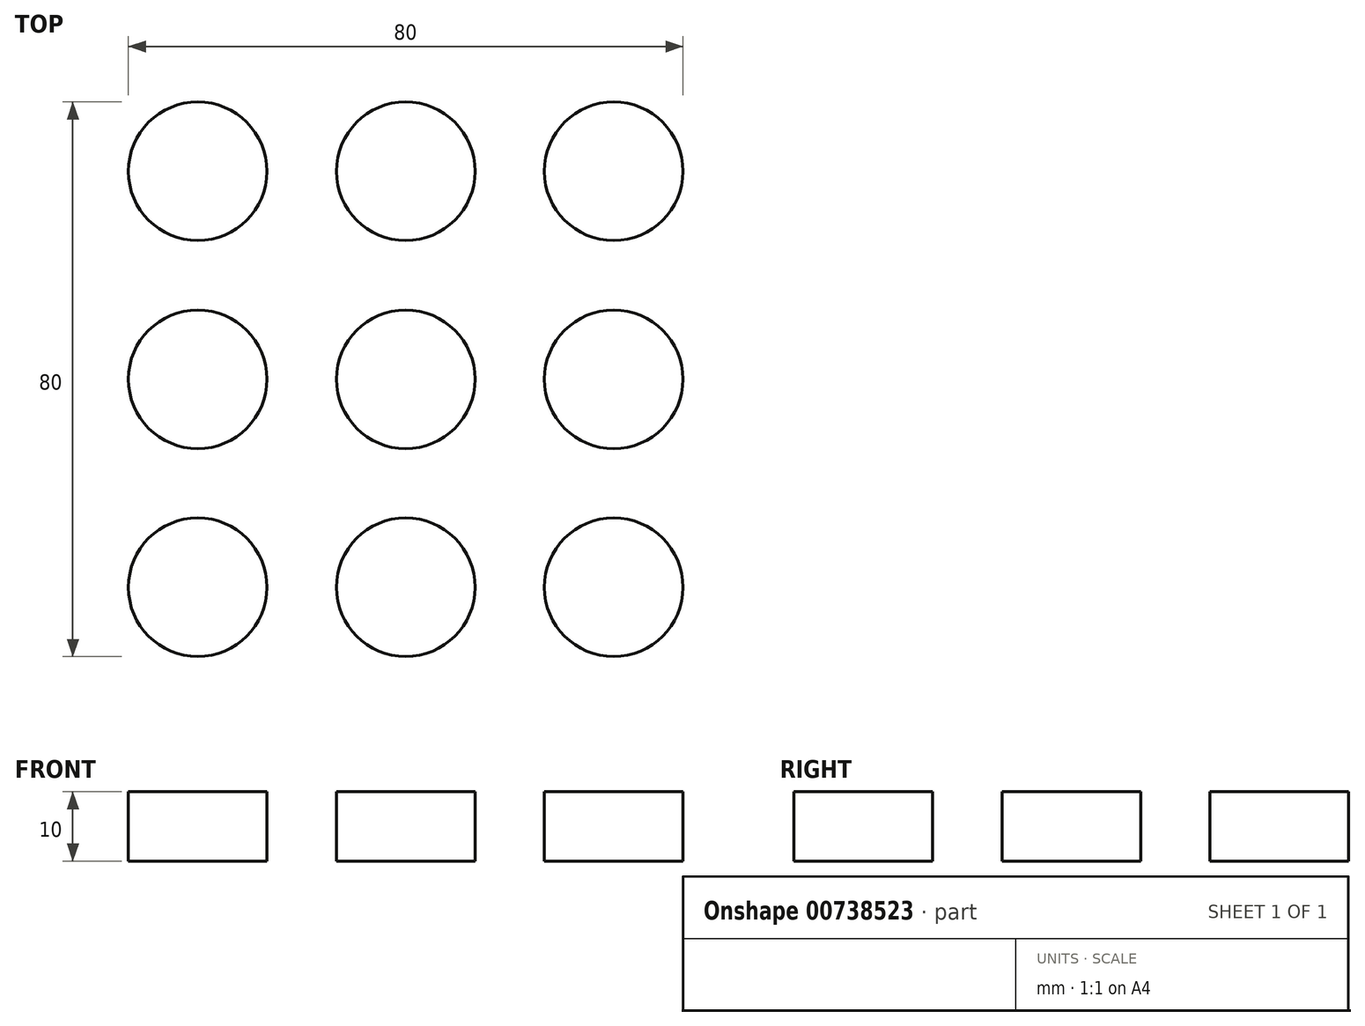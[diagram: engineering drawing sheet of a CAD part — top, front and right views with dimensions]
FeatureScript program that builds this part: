
annotation { "Feature Type Name" : "Feature", "Feature Type Description" : "" }
export const myFeature = defineFeature(function(context is Context, id is Id, definition is map)
    precondition{}
    {
        {
            var Q0;
            Q0=qCreatedBy(makeId("Top.planeOp"),FACE);
            var sketch = newSketch(context, id + "F0", { "sketchPlane" : qUnion([Q0])});
            skCircle(sketch, "E0", {"center": v(0, 0) * mm, "radius": 62.5 * mm});
            skCircle(sketch, "E1", {"center": v(0, 0) * mm, "radius": 10 * mm});
            skCircle(sketch, "E2", {"center": v(0, 30) * mm, "radius": 10 * mm});
            skCircle(sketch, "E3", {"center": v(-30, 0) * mm, "radius": 10 * mm});
            skCircle(sketch, "E4", {"center": v(-30, 30) * mm, "radius": 10 * mm});
            skCircle(sketch, "E5", {"center": v(30, 30) * mm, "radius": 10 * mm});
            skCircle(sketch, "E6", {"center": v(30, 0) * mm, "radius": 10 * mm});
            skCircle(sketch, "E7", {"center": v(30, -30) * mm, "radius": 10 * mm});
            skCircle(sketch, "E8", {"center": v(0, -30) * mm, "radius": 10 * mm});
            skCircle(sketch, "E9", {"center": v(-30, -30) * mm, "radius": 10 * mm});
            skSolve(sketch);
        }
        {
            var Q0;
            Q0=makeQuery(id+"F0.imprint","IMPRINT",FACE,{"disambiguationData":[TD([[makeQuery(id+"F0.imprint","IMPRINT",EDGE,{"derivedFrom":sQuery(id+"F0.wireOp",EDGE,"E9")}),1.0]])]});
            var Q1;
            Q1=makeQuery(id+"F0.imprint","IMPRINT",FACE,{"disambiguationData":[TD([[makeQuery(id+"F0.imprint","IMPRINT",EDGE,{"derivedFrom":sQuery(id+"F0.wireOp",EDGE,"E3")}),1.0]])]});
            var Q2;
            Q2=makeQuery(id+"F0.imprint","IMPRINT",FACE,{"disambiguationData":[TD([[makeQuery(id+"F0.imprint","IMPRINT",EDGE,{"derivedFrom":sQuery(id+"F0.wireOp",EDGE,"E4")}),1.0]])]});
            var Q3;
            Q3=makeQuery(id+"F0.imprint","IMPRINT",FACE,{"disambiguationData":[TD([[makeQuery(id+"F0.imprint","IMPRINT",EDGE,{"derivedFrom":sQuery(id+"F0.wireOp",EDGE,"E8")}),1.0]])]});
            var Q4;
            Q4=makeQuery(id+"F0.imprint","IMPRINT",FACE,{"disambiguationData":[TD([[makeQuery(id+"F0.imprint","IMPRINT",EDGE,{"derivedFrom":sQuery(id+"F0.wireOp",EDGE,"E1")}),1.0]])]});
            var Q5;
            Q5=makeQuery(id+"F0.imprint","IMPRINT",FACE,{"disambiguationData":[TD([[makeQuery(id+"F0.imprint","IMPRINT",EDGE,{"derivedFrom":sQuery(id+"F0.wireOp",EDGE,"E2")}),1.0]])]});
            var Q6;
            Q6=makeQuery(id+"F0.imprint","IMPRINT",FACE,{"disambiguationData":[TD([[makeQuery(id+"F0.imprint","IMPRINT",EDGE,{"derivedFrom":sQuery(id+"F0.wireOp",EDGE,"E5")}),1.0]])]});
            var Q7;
            Q7=makeQuery(id+"F0.imprint","IMPRINT",FACE,{"disambiguationData":[TD([[makeQuery(id+"F0.imprint","IMPRINT",EDGE,{"derivedFrom":sQuery(id+"F0.wireOp",EDGE,"E6")}),1.0]])]});
            var Q8;
            Q8=makeQuery(id+"F0.imprint","IMPRINT",FACE,{"disambiguationData":[TD([[makeQuery(id+"F0.imprint","IMPRINT",EDGE,{"derivedFrom":sQuery(id+"F0.wireOp",EDGE,"E7")}),1.0]])]});
            extrude(context, id + "F1", {"entities" : qUnion([Q0, Q1, Q2, Q3, Q4, Q5, Q6, Q7, Q8]), "depth" : 10 * mm, "offsetDistance" : 25 * mm});
        }
    });
